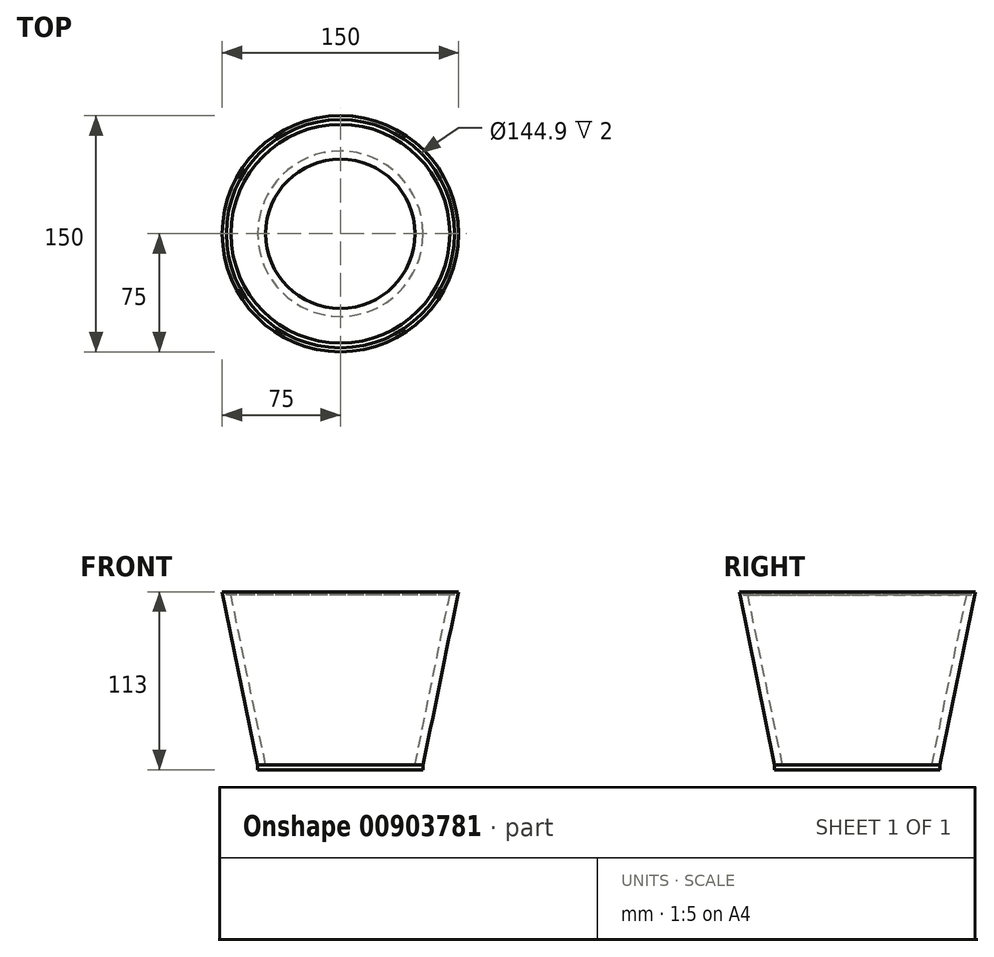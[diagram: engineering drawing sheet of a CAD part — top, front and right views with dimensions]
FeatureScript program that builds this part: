
annotation { "Feature Type Name" : "Feature", "Feature Type Description" : "" }
export const myFeature = defineFeature(function(context is Context, id is Id, definition is map)
    precondition{}
    {
        {
            var Q0;
            Q0=qCreatedBy(makeId("Front.planeOp"),FACE);
            var sketch = newSketch(context, id + "F0", { "sketchPlane" : qUnion([Q0])});
            skLineSegment(sketch, "E0", {"start": v(0, 0) * mm, "end": v(52.5, 0) * mm});
            skLineSegment(sketch, "E1", {"start": v(52.5, 0) * mm, "end": v(52.5, 3) * mm});
            skLineSegment(sketch, "E2", {"start": v(52.5, 3) * mm, "end": v(0, 3) * mm});
            skLineSegment(sketch, "E3", {"start": v(0, 3) * mm, "end": v(0, 0) * mm});
            skLineSegment(sketch, "E4", {"start": v(52.5, 3) * mm, "end": v(52.5, 113) * mm, "construction": true});
            skLineSegment(sketch, "E5", {"start": v(75, 113) * mm, "end": v(52.5, 3) * mm});
            skLineSegment(sketch, "E6", {"start": v(69.9, 113) * mm, "end": v(47.4, 3) * mm});
            skLineSegment(sketch, "E7", {"start": v(69.9, 113) * mm, "end": v(75, 113) * mm});
            skLineSegment(sketch, "E8", {"start": v(60.4, 66.53) * mm, "end": v(65.3, 65.53) * mm, "construction": true});
            skLineSegment(sketch, "E9", {"start": v(72.45, 113) * mm, "end": v(72.45, 111) * mm});
            skLineSegment(sketch, "E10", {"start": v(72.45, 111) * mm, "end": v(69.49, 111) * mm});
            skLineSegment(sketch, "E11", {"start": v(75, 113) * mm, "end": v(0, 113) * mm, "construction": true});
            skLineSegment(sketch, "E12", {"start": v(0, 113) * mm, "end": v(0, 0) * mm, "construction": true});
            skSolve(sketch);
        }
        {
            var Q0;
            Q0 = qSketchRegion(id + "F0", true);
            var Q1;
            Q1=sQuery(id+"F0.wireOp",EDGE,"E3");
            revolve(context, id + "F1", {"surfaceOperationType" : NewSurfaceOperationType.NEW, "entities" : qUnion([Q0]), "axis" : qUnion([Q1]), "revolveType" : RevolveType.FULL});
        }
        {
            var Q0;
            {var subQ4=sQuery(id+"F0.wireOp",EDGE,"E9");Q0=makeQuery(id+"F0.imprint","IMPRINT",FACE,{"disambiguationData":[TD([[makeQuery(id+"F0.imprint","IMPRINT",EDGE,{"derivedFrom":subQ4}),-1.0]])]});}
            var Q1;
            Q1=makeQuery(id+"F1.opRevolve","SWEPT_FACE",FACE,{"disambiguationData":[OSD([sQuery(id+"F0.wireOp",EDGE,"E5")])]});
            revolve(context, id + "F2", {"operationType" : NewBodyOperationType.REMOVE, "surfaceOperationType" : NewSurfaceOperationType.NEW, "entities" : qUnion([Q0]), "axis" : qUnion([Q1]), "revolveType" : RevolveType.FULL, "oppositeDirection" : true});
        }
    });
